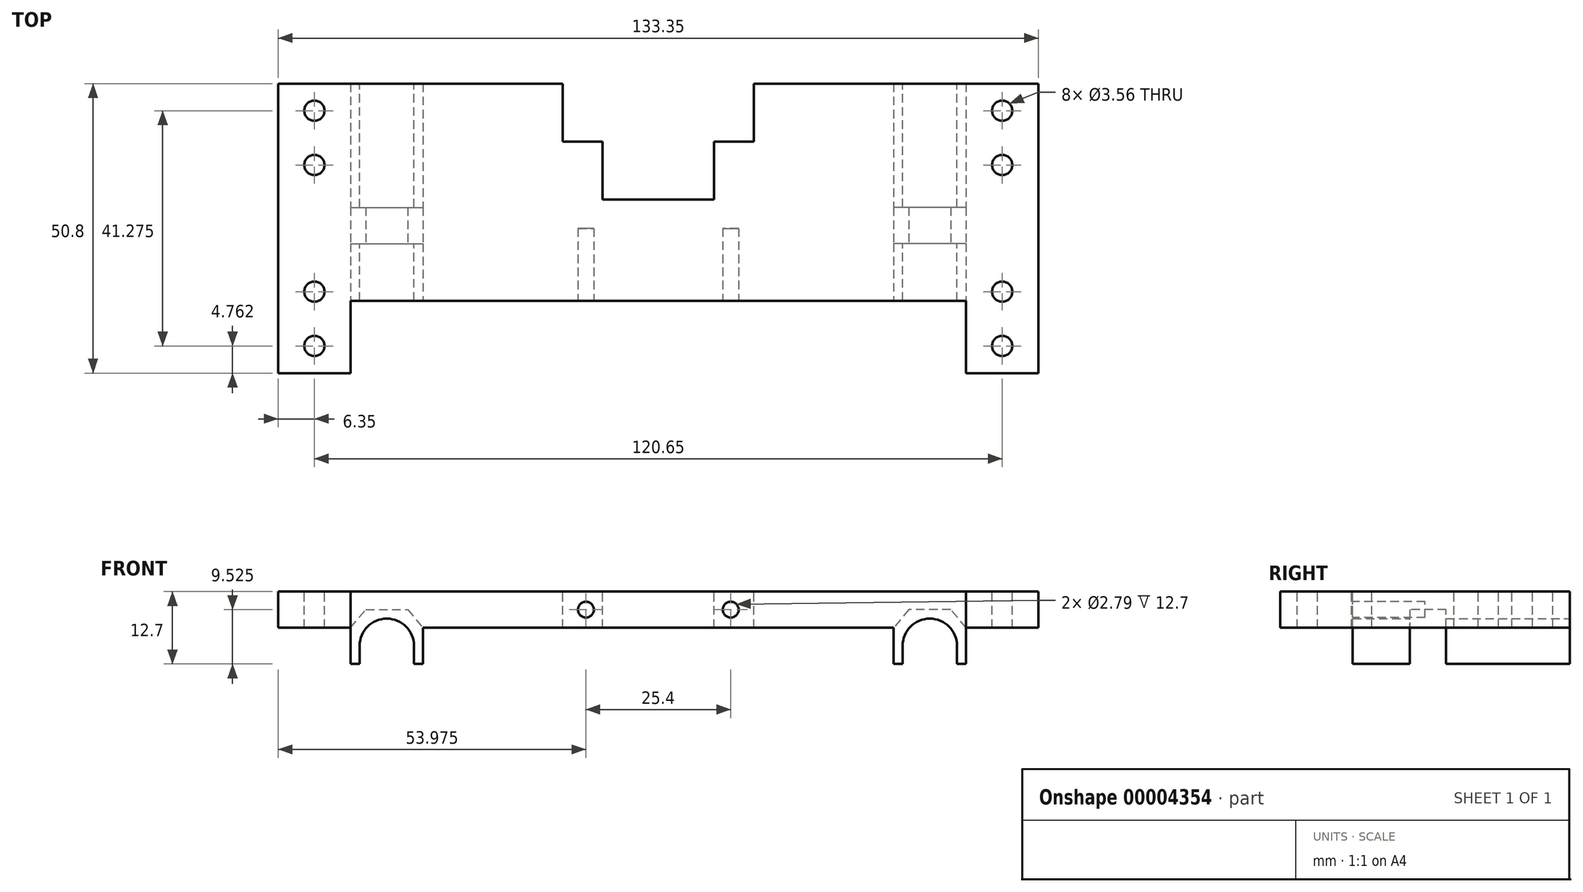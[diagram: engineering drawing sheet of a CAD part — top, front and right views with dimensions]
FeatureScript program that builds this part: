
annotation { "Feature Type Name" : "Feature", "Feature Type Description" : "" }
export const myFeature = defineFeature(function(context is Context, id is Id, definition is map)
    precondition{}
    {
        {
            var Q0;
            Q0=qCreatedBy(makeId("Top.planeOp"),FACE);
            var sketch = newSketch(context, id + "F0", { "sketchPlane" : qUnion([Q0])});
            skLineSegment(sketch, "E0.bottom", {"start": v(0, 25.4) * mm, "end": v(19.05, 25.4) * mm});
            skLineSegment(sketch, "E0.top", {"start": v(0, 0) * mm, "end": v(19.05, 0) * mm});
            skLineSegment(sketch, "E0.left", {"start": v(0, 25.4) * mm, "end": v(0, 0) * mm});
            skLineSegment(sketch, "E0.right", {"start": v(19.05, 25.4) * mm, "end": v(19.05, 0) * mm});
            skLineSegment(sketch, "E1.bottom", {"start": v(0, 6.35) * mm, "end": v(-12.7, 6.35) * mm});
            skLineSegment(sketch, "E1.top", {"start": v(0, 25.4) * mm, "end": v(-12.7, 25.4) * mm});
            skLineSegment(sketch, "E1.left", {"start": v(0, 6.35) * mm, "end": v(0, 25.4) * mm});
            skLineSegment(sketch, "E1.right", {"start": v(-12.7, 6.35) * mm, "end": v(-12.7, 25.4) * mm});
            skLineSegment(sketch, "E2.rect.bottom", {"start": v(17.63, 25.4) * mm, "end": v(1.76, 25.4) * mm, "construction": true});
            skLineSegment(sketch, "E2.rect.top", {"start": v(17.63, 0) * mm, "end": v(1.76, 0) * mm, "construction": true});
            skCircle(sketch, "E3", {"center": v(-6.35, 20.64) * mm, "radius": 1.78 * mm});
            skCircle(sketch, "E4", {"center": v(-6.35, 11.11) * mm, "radius": 1.78 * mm});
            skLineSegment(sketch, "E5", {"start": v(-6.35, 25.4) * mm, "end": v(-6.35, 6.35) * mm, "construction": true});
            skPoint(sketch, "E6", {"position": v(-6.35, 15.87) * mm});
            skLineSegment(sketch, "E7", {"start": v(-6.35, 11.11) * mm, "end": v(-6.35, 20.64) * mm, "construction": true});
            skLineSegment(sketch, "E8.0.MirrorCS", {"start": v(17.63, -25.4) * mm, "end": v(1.76, -25.4) * mm, "construction": true});
            skLineSegment(sketch, "E8.1.MirrorCS", {"start": v(-6.35, -11.11) * mm, "end": v(-6.35, -20.64) * mm, "construction": true});
            skLineSegment(sketch, "E8.3.MirrorCS", {"start": v(0, -25.4) * mm, "end": v(19.05, -25.4) * mm});
            skLineSegment(sketch, "E8.4.MirrorCS", {"start": v(0, -25.4) * mm, "end": v(0, 0) * mm});
            skLineSegment(sketch, "E8.5.MirrorCS", {"start": v(0, -6.35) * mm, "end": v(-12.7, -6.35) * mm});
            skLineSegment(sketch, "E8.6.MirrorCS", {"start": v(19.05, -25.4) * mm, "end": v(19.05, 0) * mm});
            skLineSegment(sketch, "E8.7.MirrorCS", {"start": v(0, -6.35) * mm, "end": v(0, -25.4) * mm});
            skLineSegment(sketch, "E8.8.MirrorCS", {"start": v(0, -25.4) * mm, "end": v(-12.7, -25.4) * mm});
            skLineSegment(sketch, "E8.9.MirrorCS", {"start": v(-12.7, -6.35) * mm, "end": v(-12.7, -25.4) * mm});
            skCircle(sketch, "E8.10.MirrorC", {"center": v(-6.35, -20.64) * mm, "radius": 1.78 * mm});
            skPoint(sketch, "E8.11.MirrorP", {"position": v(-6.35, -15.87) * mm});
            skCircle(sketch, "E8.12.MirrorC", {"center": v(-6.35, -11.11) * mm, "radius": 1.78 * mm});
            skLineSegment(sketch, "E8.13.MirrorCS", {"start": v(-6.35, -25.4) * mm, "end": v(-6.35, -6.35) * mm, "construction": true});
            skSolve(sketch);
        }
        {
            var Q0;
            Q0=qCreatedBy(makeId("Top.planeOp"),FACE);
            var sketch = newSketch(context, id + "F1", { "sketchPlane" : qUnion([Q0])});
            skLineSegment(sketch, "E9.bottom", {"start": v(0, -25.4) * mm, "end": v(-66.68, -25.4) * mm});
            skLineSegment(sketch, "E9.top", {"start": v(0, 25.4) * mm, "end": v(-66.68, 25.4) * mm});
            skLineSegment(sketch, "E9.left", {"start": v(0, -25.4) * mm, "end": v(0, 25.4) * mm});
            skLineSegment(sketch, "E9.right", {"start": v(-66.68, -25.4) * mm, "end": v(-66.68, 25.4) * mm});
            skPoint(sketch, "E10", {"position": v(9.52, -25.4) * mm});
            skCircle(sketch, "E11", {"center": v(-6.35, 20.64) * mm, "radius": 1.78 * mm});
            skCircle(sketch, "E12", {"center": v(-6.35, 11.11) * mm, "radius": 1.78 * mm});
            skCircle(sketch, "E13", {"center": v(-6.35, -11.11) * mm, "radius": 1.78 * mm});
            skCircle(sketch, "E14", {"center": v(-6.35, -20.64) * mm, "radius": 1.78 * mm});
            skLineSegment(sketch, "E15", {"start": v(-12.7, -25.4) * mm, "end": v(-12.7, -12.7) * mm});
            skLineSegment(sketch, "E16", {"start": v(-12.7, -12.7) * mm, "end": v(-66.68, -12.7) * mm});
            skLineSegment(sketch, "E17.top", {"start": v(-66.68, 15.24) * mm, "end": v(-49.91, 15.24) * mm});
            skLineSegment(sketch, "E17.right", {"start": v(-49.91, 25.4) * mm, "end": v(-49.91, 15.24) * mm});
            skLineSegment(sketch, "E18", {"start": v(-49.91, 15.24) * mm, "end": v(-49.91, -12.7) * mm});
            skLineSegment(sketch, "E19", {"start": v(-49.91, -12.7) * mm, "end": v(-66.68, -12.7) * mm});
            skLineSegment(sketch, "E20", {"start": v(-56.9, 15.24) * mm, "end": v(-56.9, 5.08) * mm});
            skLineSegment(sketch, "E21", {"start": v(-56.9, 5.08) * mm, "end": v(-66.68, 5.08) * mm});
            skCircle(sketch, "E22", {"center": v(-61.79, 0.95) * mm, "radius": 1.78 * mm});
            skCircle(sketch, "E23", {"center": v(-61.79, -8.57) * mm, "radius": 1.78 * mm});
            skLineSegment(sketch, "E24", {"start": v(-61.79, 0.95) * mm, "end": v(-61.79, -8.57) * mm, "construction": true});
            skLineSegment(sketch, "E25", {"start": v(-61.79, 0.95) * mm, "end": v(-61.79, 5.08) * mm, "construction": true});
            skLineSegment(sketch, "E26", {"start": v(-61.79, -8.57) * mm, "end": v(-61.79, -12.7) * mm, "construction": true});
            skSolve(sketch);
        }
        {
            var Q0;
            {var subQ3=sQuery(id+"F1.wireOp",EDGE,"E18");Q0=makeQuery(id+"F1.imprint","IMPRINT",FACE,{"disambiguationData":[TD([[makeQuery(id+"F1.imprint","IMPRINT",EDGE,{"derivedFrom":subQ3}),-1.0]])]});}
            var Q1;
            {var subQ5=sQuery(id+"F1.wireOp",EDGE,"E9.left");Q1=makeQuery(id+"F1.imprint","IMPRINT",FACE,{"disambiguationData":[TD([[makeQuery(id+"F1.imprint","IMPRINT",EDGE,{"derivedFrom":subQ5}),1.0]])]});}
            var Q2;
            Q2=makeQuery(id+"F1.imprint","IMPRINT",FACE,{"disambiguationData":[TD([[makeQuery(id+"F1.imprint","IMPRINT",EDGE,{"derivedFrom":sQuery(id+"F1.wireOp",EDGE,"E22")}),1.0]])]});
            var Q3;
            Q3=makeQuery(id+"F1.imprint","IMPRINT",FACE,{"disambiguationData":[TD([[makeQuery(id+"F1.imprint","IMPRINT",EDGE,{"derivedFrom":sQuery(id+"F1.wireOp",EDGE,"E23")}),1.0]])]});
            var Q4;
            Q4=makeQuery(id+"F1.imprint","IMPRINT",FACE,{"disambiguationData":[TD([[makeQuery(id+"F1.imprint","IMPRINT",EDGE,{"derivedFrom":sQuery(id+"F1.wireOp",EDGE,"ab8138ad-efc8-401e-9fac-4fe4797554c6.bottom")}),1.0]])]});
            var Q5;
            Q5=makeQuery(id+"F1.imprint","IMPRINT",FACE,{"disambiguationData":[TD([[makeQuery(id+"F1.imprint","IMPRINT",EDGE,{"derivedFrom":sQuery(id+"F1.wireOp",EDGE,"E16")}),-1.0]])]});
            var Q6;
            Q6=sQuery(id+"F1.wireOp",EDGE,"E9.right");
            var Q7;
            Q7=sQuery(id+"F1.wireOp",EDGE,"E9.bottom");
            var Q8;
            Q8=sQuery(id+"F1.wireOp",EDGE,"E9.top");
            var Q9;
            Q9=sQuery(id+"F1.wireOp",EDGE,"E9.left");
            extrude(context, id + "F2", {"entities" : qUnion([Q0, Q1, Q2, Q3, Q4, Q5]), "surfaceEntities" : qUnion([Q6, Q7, Q8, Q9]), "oppositeDirection" : true, "depth" : 6.35 * mm});
        }
        {
            var Q0;
            Q0=makeQuery(id+"F2.opExtrude","SWEPT_FACE",FACE,{"disambiguationData":[OSD([sQuery(id+"F1.wireOp",EDGE,"E16"),sQuery(id+"F1.wireOp",EDGE,"E19")])]});
            var sketch = newSketch(context, id + "F3", { "sketchPlane" : qUnion([Q0])});
            skCircle(sketch, "E27", {"center": v(-53.98, -3.17) * mm, "radius": 1.4 * mm});
            skLineSegment(sketch, "E28", {"start": v(-53.98, 0) * mm, "end": v(-53.98, -6.35) * mm, "construction": true});
            skSolve(sketch);
        }
        {
            var Q0;
            Q0=makeQuery(id+"F3.imprint","IMPRINT",FACE,{"disambiguationData":[TD([[makeQuery(id+"F3.imprint","IMPRINT",EDGE,{"derivedFrom":sQuery(id+"F3.wireOp",EDGE,"E27")}),1.0]])]});
            extrude(context, id + "F4", {"entities" : qUnion([Q0]), "operationType" : NewBodyOperationType.REMOVE, "oppositeDirection" : true, "depth" : 12.7 * mm});
        }
        {
            var Q0;
            Q0=makeQuery(id+"F2.opExtrude","CAP_FACE",FACE,{"disambiguationData":[OSD([sQuery(id+"F1.wireOp",EDGE,"E9.bottom"),sQuery(id+"F1.wireOp",EDGE,"E9.top"),sQuery(id+"F1.wireOp",EDGE,"E9.left"),sQuery(id+"F1.wireOp",EDGE,"E9.right"),sQuery(id+"F1.wireOp",EDGE,"E11"),sQuery(id+"F1.wireOp",EDGE,"E12"),sQuery(id+"F1.wireOp",EDGE,"E13"),sQuery(id+"F1.wireOp",EDGE,"E14"),sQuery(id+"F1.wireOp",EDGE,"E15"),sQuery(id+"F1.wireOp",EDGE,"E16"),sQuery(id+"F1.wireOp",EDGE,"E17.top"),sQuery(id+"F1.wireOp",EDGE,"E17.right"),sQuery(id+"F1.wireOp",EDGE,"E19"),sQuery(id+"F1.wireOp",EDGE,"E20"),sQuery(id+"F1.wireOp",EDGE,"E21")])],"isStart":false});
            var sketch = newSketch(context, id + "F5", { "sketchPlane" : qUnion([Q0])});
            skLineSegment(sketch, "E29.bottom", {"start": v(-25.4, -25.4) * mm, "end": v(-12.7, -25.4) * mm});
            skLineSegment(sketch, "E29.top", {"start": v(-25.4, 12.7) * mm, "end": v(-12.7, 12.7) * mm});
            skLineSegment(sketch, "E29.left", {"start": v(-25.4, -25.4) * mm, "end": v(-25.4, 12.7) * mm});
            skLineSegment(sketch, "E29.right", {"start": v(-12.7, -25.4) * mm, "end": v(-12.7, 12.7) * mm});
            skSolve(sketch);
        }
        {
            var Q0;
            Q0=makeQuery(id+"F5.imprint","IMPRINT",FACE,{"disambiguationData":[TD([[makeQuery(id+"F5.imprint","IMPRINT",EDGE,{"derivedFrom":sQuery(id+"F5.wireOp",EDGE,"E29.bottom")}),-1.0]])]});
            extrude(context, id + "F6", {"entities" : qUnion([Q0]), "operationType" : NewBodyOperationType.ADD, "depth" : 6.35 * mm});
        }
        {
            var Q0;
            Q0=makeQuery(id+"F6.boolean.opBoolean","MERGE",FACE,{"derivedFrom":[makeQuery(id+"F2.opExtrude","SWEPT_FACE",FACE,{"disambiguationData":[OSD([sQuery(id+"F1.wireOp",EDGE,"E9.top")])]}),makeQuery(id+"F6.opExtrude","SWEPT_FACE",FACE,{"disambiguationData":[OSD([sQuery(id+"F5.wireOp",EDGE,"E29.bottom")])]})]});
            var sketch = newSketch(context, id + "F7", { "sketchPlane" : qUnion([Q0])});
            skLineSegment(sketch, "E30", {"start": v(19.05, -12.7) * mm, "end": v(19.05, -6.35) * mm, "construction": true});
            skCircle(sketch, "E31", {"center": v(19.05, -9.53) * mm, "radius": 3.18 * mm, "construction": true});
            skCircle(sketch, "E32", {"center": v(19.05, -9.53) * mm, "radius": 4.76 * mm});
            skCircle(sketch, "E33", {"center": v(19.05, -9.53) * mm, "radius": 6.35 * mm, "construction": true});
            skLineSegment(sketch, "E34.0", {"start": v(15.38, -3.17) * mm, "end": v(22.72, -3.17) * mm});
            skLineSegment(sketch, "E34.1", {"start": v(22.72, -3.17) * mm, "end": v(26.38, -9.53) * mm, "construction": true});
            skLineSegment(sketch, "E34.2", {"start": v(26.38, -9.53) * mm, "end": v(22.72, -15.88) * mm, "construction": true});
            skLineSegment(sketch, "E34.3", {"start": v(22.72, -15.88) * mm, "end": v(15.38, -15.88) * mm, "construction": true});
            skLineSegment(sketch, "E34.4", {"start": v(15.38, -15.88) * mm, "end": v(11.72, -9.53) * mm, "construction": true});
            skLineSegment(sketch, "E34.5", {"start": v(11.72, -9.53) * mm, "end": v(15.38, -3.17) * mm, "construction": true});
            skPoint(sketch, "E34.0.midPoint", {"position": v(19.05, -3.17) * mm});
            skLineSegment(sketch, "E35", {"start": v(19.05, -9.53) * mm, "end": v(14.29, -9.53) * mm, "construction": true});
            skLineSegment(sketch, "E36", {"start": v(19.05, -9.53) * mm, "end": v(23.81, -9.53) * mm, "construction": true});
            skLineSegment(sketch, "E37", {"start": v(14.29, -9.53) * mm, "end": v(14.29, -12.7) * mm});
            skLineSegment(sketch, "E38", {"start": v(23.81, -9.53) * mm, "end": v(23.81, -12.7) * mm});
            skLineSegment(sketch, "E39", {"start": v(22.72, -3.17) * mm, "end": v(25.4, -6.35) * mm});
            skLineSegment(sketch, "E40", {"start": v(25.4, -6.35) * mm, "end": v(25.4, -7.82) * mm});
            skLineSegment(sketch, "E41", {"start": v(15.38, -3.17) * mm, "end": v(12.7, -6.35) * mm});
            skLineSegment(sketch, "E42", {"start": v(12.7, -6.35) * mm, "end": v(12.7, -7.82) * mm});
            skSolve(sketch);
        }
        {
            var Q0;
            Q0=makeQuery(id+"F7.imprint","IMPRINT",FACE,{"disambiguationData":[TD([[makeQuery(id+"F7.imprint","IMPRINT",EDGE,{"derivedFrom":sQuery(id+"F7.wireOp",EDGE,"4880f42c-5ce7-493f-9680-80e75f1e6eee")}),1.0]])]});
            var Q1;
            {var subQ2=sQuery(id+"F7.wireOp",EDGE,"3b5a587a-ce11-4dcc-bb01-76d29c6a4fb7");Q1=makeQuery(id+"F7.imprint","IMPRINT",FACE,{"disambiguationData":[TD([[makeQuery(id+"F7.imprint","IMPRINT",EDGE,{"derivedFrom":subQ2}),1.0]])]});}
            var Q2;
            {var subQ1=sQuery(id+"F7.wireOp",EDGE,"E32");var subQ5=makeQuery(id+"F7.imprint","INTERSECT",VERTEX,{"derivedFrom":[subQ1,sQuery(id+"F7.wireOp",EDGE,"E37")]});Q2=makeQuery(id+"F7.imprint","IMPRINT",FACE,{"disambiguationData":[TD([[makeQuery(id+"F7.imprint","IMPRINT",EDGE,{"disambiguationData":[TD([[subQ5,1.0]])],"derivedFrom":subQ1}),1.0]])]});}
            var Q3;
            {var subQ3=sQuery(id+"F7.wireOp",EDGE,"E38");Q3=makeQuery(id+"F7.imprint","IMPRINT",FACE,{"disambiguationData":[TD([[makeQuery(id+"F7.imprint","IMPRINT",EDGE,{"derivedFrom":subQ3}),-1.0]])]});}
            var Q4;
            {var subQ3=sQuery(id+"F7.wireOp",EDGE,"E37");Q4=makeQuery(id+"F7.imprint","IMPRINT",FACE,{"disambiguationData":[TD([[makeQuery(id+"F7.imprint","IMPRINT",EDGE,{"derivedFrom":subQ3}),1.0]])]});}
            extrude(context, id + "F8", {"entities" : qUnion([Q0, Q1, Q2, Q3, Q4]), "operationType" : NewBodyOperationType.REMOVE, "endBound" : BoundingType.THROUGH_ALL, "oppositeDirection" : true, "depth" : 25.4 * mm});
        }
        {
            var Q0;
            Q0=sQuery(id+"F7.wireOp",EDGE,"E39");
            var Q1;
            Q1=sQuery(id+"F7.wireOp",EDGE,"E34.0");
            var Q2;
            Q2=sQuery(id+"F7.wireOp",EDGE,"E41");
            extrude(context, id + "F9", {"bodyType" : ExtendedToolBodyType.SURFACE, "surfaceEntities" : qUnion([Q0, Q1, Q2]), "endBound" : BoundingType.UP_TO_NEXT, "oppositeDirection" : true, "depth" : 25.4 * mm});
        }
        {
            var Q0;
            Q0=makeQuery(id+"F6.opExtrude","CAP_FACE",FACE,{"disambiguationData":[OSD([sQuery(id+"F5.wireOp",EDGE,"E29.bottom"),sQuery(id+"F5.wireOp",EDGE,"E29.top"),sQuery(id+"F5.wireOp",EDGE,"E29.left"),sQuery(id+"F5.wireOp",EDGE,"E29.right")])],"isStart":false});
            var sketch = newSketch(context, id + "F10", { "sketchPlane" : qUnion([Q0])});
            skPoint(sketch, "E43", {"position": v(-24.6, 12.7) * mm});
            skPoint(sketch, "E44", {"position": v(-24.6, -25.4) * mm});
            skLineSegment(sketch, "E45", {"start": v(-24.6, 12.7) * mm, "end": v(-24.6, -25.4) * mm, "construction": true});
            skLineSegment(sketch, "E46.bottom", {"start": v(-12.7, -3.67) * mm, "end": v(-25.4, -3.67) * mm});
            skLineSegment(sketch, "E46.top", {"start": v(-12.7, 2.68) * mm, "end": v(-25.4, 2.68) * mm});
            skLineSegment(sketch, "E46.left", {"start": v(-12.7, -3.67) * mm, "end": v(-12.7, 2.68) * mm});
            skLineSegment(sketch, "E46.right", {"start": v(-25.4, -3.67) * mm, "end": v(-25.4, 2.68) * mm});
            skSolve(sketch);
        }
        {
            var Q0;
            {var subQ5=sQuery(id+"F10.wireOp",EDGE,"E46.left");Q0=makeQuery(id+"F10.imprint","IMPRINT",FACE,{"disambiguationData":[TD([[makeQuery(id+"F10.imprint","IMPRINT",EDGE,{"derivedFrom":subQ5}),1.0]])]});}
            var Q1;
            {var subQ0=sQuery(id+"F5.wireOp",EDGE,"E29.bottom");var subQ4=sQuery(id+"F10.wireOp",EDGE,"E46.bottom");var subQ6=makeQuery(id+"F8.boolean.opBoolean","COPY",EDGE,{"derivedFrom":makeQuery(id+"F8.opExtrude","SWEPT_EDGE",EDGE,{"disambiguationData":[OSD([subQ0,sQuery(id+"F7.wireOp",EDGE,"E37")])]})});var subQ8=makeQuery(id+"F10.imprint","INTERSECT",VERTEX,{"derivedFrom":[subQ6,subQ4]});Q1=makeQuery(id+"F10.imprint","IMPRINT",FACE,{"disambiguationData":[TD([[makeQuery(id+"F10.imprint","IMPRINT",EDGE,{"disambiguationData":[TD([[subQ8,-1.0]])],"derivedFrom":subQ4}),-1.0]])]});}
            var Q2;
            {var subQ5=sQuery(id+"F10.wireOp",EDGE,"E46.right");Q2=makeQuery(id+"F10.imprint","IMPRINT",FACE,{"disambiguationData":[TD([[makeQuery(id+"F10.imprint","IMPRINT",EDGE,{"derivedFrom":subQ5}),-1.0]])]});}
            var Q3;
            Q3=makeQuery(id+"F9.opExtrude","SWEPT_BODY",BODY,{"disambiguationData":[OSD([sQuery(id+"F7.wireOp",EDGE,"E41")])]});
            extrude(context, id + "F11", {"entities" : qUnion([Q0, Q1, Q2]), "operationType" : NewBodyOperationType.REMOVE, "endBound" : BoundingType.UP_TO_BODY, "oppositeDirection" : true, "endBoundEntityBody" : qUnion([Q3]), "depth" : 25.4 * mm});
        }
        {
            var Q0;
            Q0=makeQuery(id+"F2.opExtrude","SWEPT_BODY",BODY,{"disambiguationData":[OSD([sQuery(id+"F1.wireOp",EDGE,"E9.bottom"),sQuery(id+"F1.wireOp",EDGE,"E9.top"),sQuery(id+"F1.wireOp",EDGE,"E9.left"),sQuery(id+"F1.wireOp",EDGE,"E9.right"),sQuery(id+"F1.wireOp",EDGE,"E11"),sQuery(id+"F1.wireOp",EDGE,"E12"),sQuery(id+"F1.wireOp",EDGE,"E13"),sQuery(id+"F1.wireOp",EDGE,"E14")])]});
            var Q1;
            Q1=makeQuery(id+"F2.opExtrude","SWEPT_FACE",FACE,{"disambiguationData":[OSD([sQuery(id+"F1.wireOp",EDGE,"E9.right")])]});
            mirror(context, id + "F12", {"operationType" : NewBodyOperationType.ADD, "entities" : qUnion([Q0]), "mirrorPlane" : qUnion([Q1])});
        }
    });
